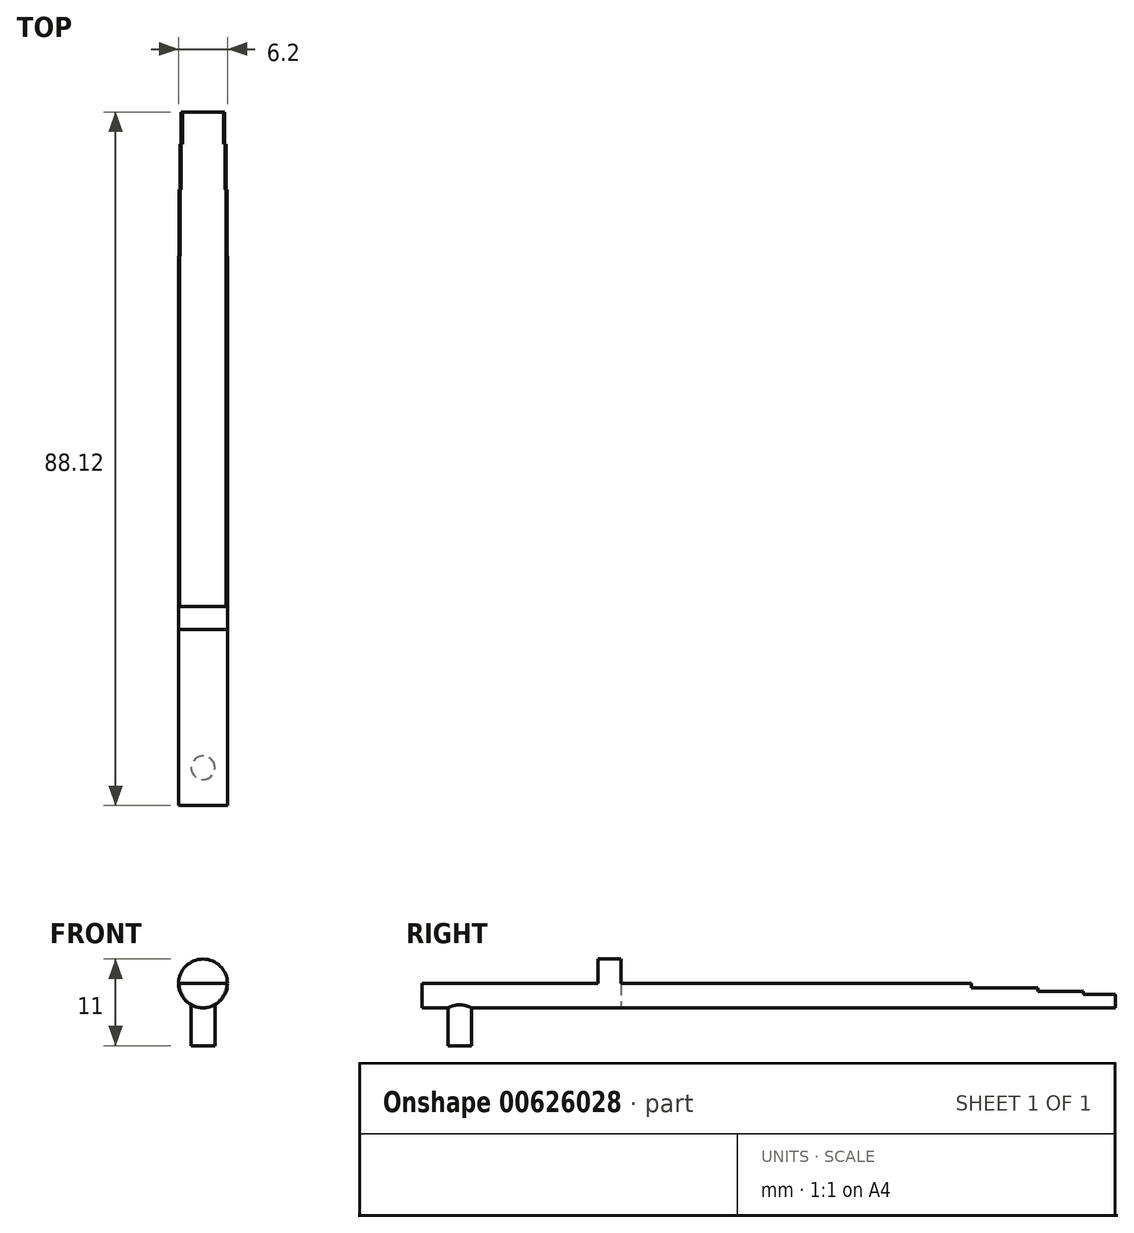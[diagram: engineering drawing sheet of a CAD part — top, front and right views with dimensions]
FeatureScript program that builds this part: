
annotation { "Feature Type Name" : "Feature", "Feature Type Description" : "" }
export const myFeature = defineFeature(function(context is Context, id is Id, definition is map)
    precondition{}
    {
        {
            var Q0;
            Q0=qCreatedBy(makeId("Front.planeOp"),FACE);
            var sketch = newSketch(context, id + "F0", { "sketchPlane" : qUnion([Q0])});
            skCircle(sketch, "E0", {"center": v(0, 0) * mm, "radius": 3.1 * mm});
            skSolve(sketch);
        }
        {
            var Q0;
            Q0 = qSketchRegion(id + "F0", true);
            extrude(context, id + "F1", {"entities" : qUnion([Q0]), "depth" : 88.12 * mm, "offsetDistance" : 25 * mm});
        }
        {
            var Q0;
            Q0=makeQuery(id+"F1.opExtrude","CAP_FACE",FACE,{"disambiguationData":[OSD([sQuery(id+"F0.wireOp",EDGE,"E0")])],"isStart":false});
            var sketch = newSketch(context, id + "F2", { "sketchPlane" : qUnion([Q0])});
            skLineSegment(sketch, "E1", {"start": v(-3.1, 0) * mm, "end": v(3.1, 0) * mm});
            skArc(sketch, "E2", {"start": v(3.1, 0) * mm, "mid": v(0, 3.1) * mm, "end": v(-3.1, 0) * mm});
            skSolve(sketch);
        }
        {
            var Q0;
            Q0 = qSketchRegion(id + "F2", true);
            extrude(context, id + "F3", {"entities" : qUnion([Q0]), "operationType" : NewBodyOperationType.REMOVE, "oppositeDirection" : true, "depth" : 22.4 * mm, "offsetDistance" : 25 * mm});
        }
        {
            var Q0;
            Q0=makeQuery(id+"F1.opExtrude","CAP_FACE",FACE,{"disambiguationData":[OSD([sQuery(id+"F0.wireOp",EDGE,"E0")])],"isStart":true});
            var sketch = newSketch(context, id + "F4", { "sketchPlane" : qUnion([Q0])});
            skLineSegment(sketch, "E3", {"start": v(-3.1, 0) * mm, "end": v(3.1, 0) * mm});
            skArc(sketch, "E4", {"start": v(3.1, 0) * mm, "mid": v(0, 3.1) * mm, "end": v(-3.1, 0) * mm});
            skSolve(sketch);
        }
        {
            var Q0;
            Q0 = qSketchRegion(id + "F4", true);
            extrude(context, id + "F5", {"entities" : qUnion([Q0]), "operationType" : NewBodyOperationType.REMOVE, "oppositeDirection" : true, "depth" : 62.8 * mm, "offsetDistance" : 25 * mm});
        }
        {
            var Q0;
            Q0=makeQuery(id+"F1.opExtrude","CAP_FACE",FACE,{"disambiguationData":[OSD([sQuery(id+"F0.wireOp",EDGE,"E0")])],"isStart":true});
            var sketch = newSketch(context, id + "F6", { "sketchPlane" : qUnion([Q0])});
            skCircle(sketch, "E5", {"center": v(0, 0) * mm, "radius": 2.95 * mm});
            skSolve(sketch);
        }
        {
            var Q0;
            Q0 = qSketchRegion(id + "F6", true);
            extrude(context, id + "F7", {"entities" : qUnion([Q0]), "operationType" : NewBodyOperationType.REMOVE, "oppositeDirection" : true, "depth" : 62.8 * mm, "offsetDistance" : 25 * mm});
        }
        {
            var Q0;
            Q0=qCreatedBy(makeId("Right.planeOp"),FACE);
            var sketch = newSketch(context, id + "F8", { "sketchPlane" : qUnion([Q0])});
            skLineSegment(sketch, "E6", {"start": v(-18.3, 0) * mm, "end": v(-18.3, -0.55) * mm});
            skLineSegment(sketch, "E7", {"start": v(-18.3, -0.55) * mm, "end": v(-9.9, -0.55) * mm});
            skLineSegment(sketch, "E8", {"start": v(-9.9, -0.55) * mm, "end": v(-9.9, -1) * mm});
            skLineSegment(sketch, "E9", {"start": v(-9.9, -1) * mm, "end": v(-4.1, -1) * mm});
            skLineSegment(sketch, "E10", {"start": v(-4.1, -1) * mm, "end": v(-4.1, -1.4) * mm});
            skLineSegment(sketch, "E11", {"start": v(-4.1, -1.4) * mm, "end": v(0, -1.4) * mm});
            skLineSegment(sketch, "E12", {"start": v(0, -1.4) * mm, "end": v(0, 0) * mm});
            skLineSegment(sketch, "E13", {"start": v(0, 0) * mm, "end": v(-18.3, 0) * mm});
            skSolve(sketch);
        }
        {
            var Q0;
            Q0 = qSketchRegion(id + "F8", true);
            extrude(context, id + "F9", {"entities" : qUnion([Q0]), "operationType" : NewBodyOperationType.REMOVE, "oppositeDirection" : true, "depth" : 25 * mm, "offsetDistance" : 25 * mm, "symmetric" : true});
        }
        {
            var Q0;
            Q0=makeQuery(id+"F3.boolean.opBoolean","COPY",FACE,{"derivedFrom":makeQuery(id+"F3.opExtrude","SWEPT_FACE",FACE,{"disambiguationData":[OSD([sQuery(id+"F2.wireOp",EDGE,"E1")])]})});
            var sketch = newSketch(context, id + "F10", { "sketchPlane" : qUnion([Q0])});
            skCircle(sketch, "E14", {"center": v(0, -83.32) * mm, "radius": 1.5 * mm});
            skSolve(sketch);
        }
        {
            var Q0;
            Q0 = qSketchRegion(id + "F10", true);
            extrude(context, id + "F11", {"entities" : qUnion([Q0]), "operationType" : NewBodyOperationType.ADD, "oppositeDirection" : true, "depth" : 7.9 * mm, "offsetDistance" : 25 * mm});
        }
    });
